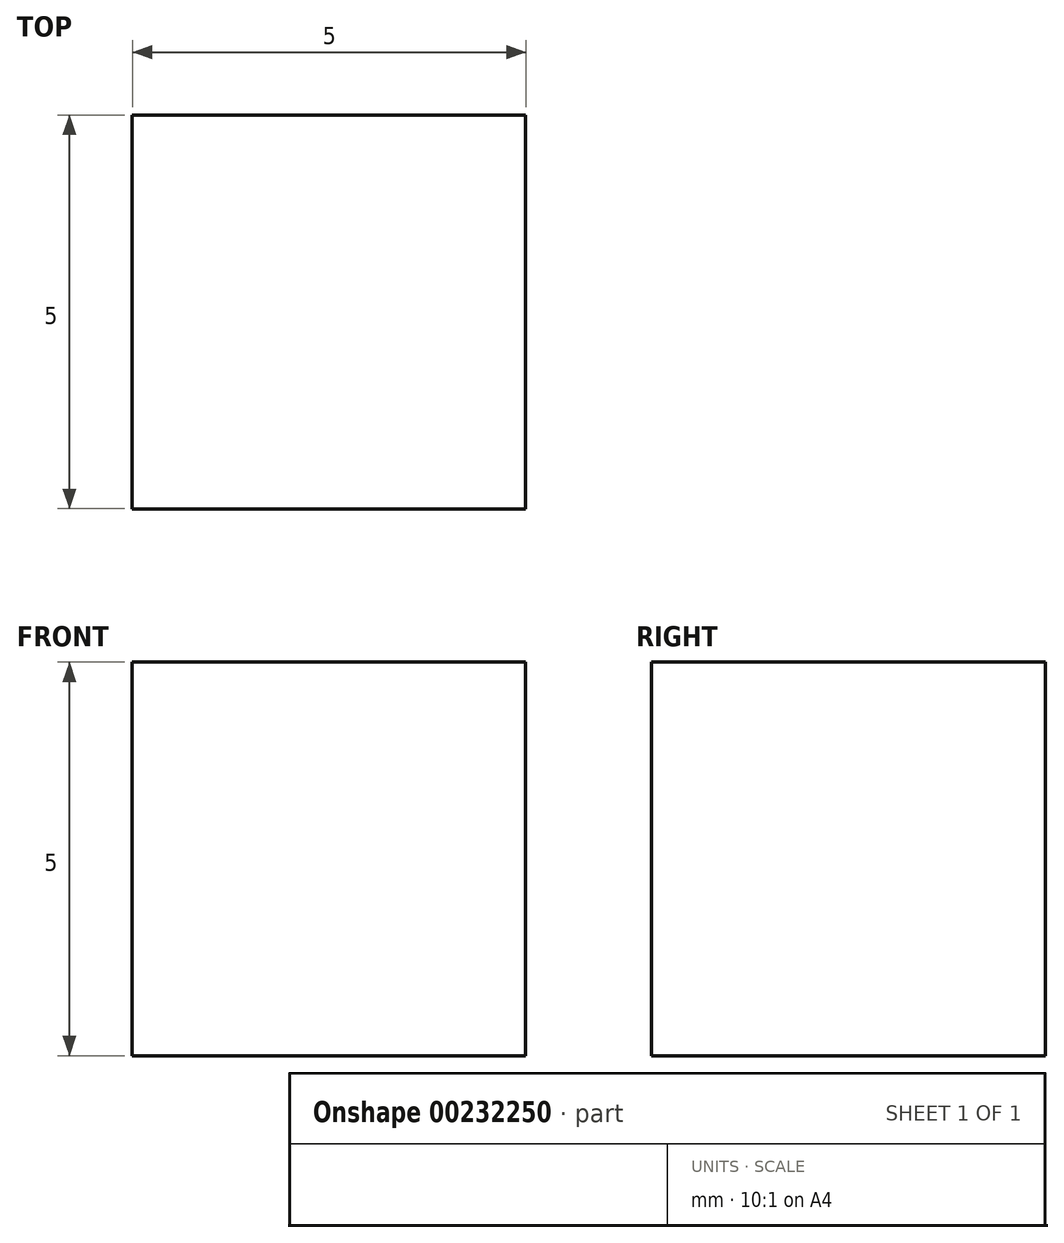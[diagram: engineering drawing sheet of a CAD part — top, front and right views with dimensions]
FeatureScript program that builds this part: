
annotation { "Feature Type Name" : "Feature", "Feature Type Description" : "" }
export const myFeature = defineFeature(function(context is Context, id is Id, definition is map)
    precondition{}
    {
        {
            var Q0;
            Q0=qCreatedBy(makeId("Top.planeOp"),FACE);
            var sketch = newSketch(context, id + "F0", { "sketchPlane" : qUnion([Q0])});
            skLineSegment(sketch, "E0.bottom", {"start": v(-14.38, 18.95) * mm, "end": v(-9.38, 18.95) * mm});
            skLineSegment(sketch, "E0.top", {"start": v(-14.38, 13.95) * mm, "end": v(-9.38, 13.95) * mm});
            skLineSegment(sketch, "E0.left", {"start": v(-14.38, 18.95) * mm, "end": v(-14.38, 13.95) * mm});
            skLineSegment(sketch, "E0.right", {"start": v(-9.38, 18.95) * mm, "end": v(-9.38, 13.95) * mm});
            skSolve(sketch);
        }
        {
            var Q0;
            Q0=makeQuery(id+"F0.imprint","IMPRINT",FACE,{"disambiguationData":[TD([[makeQuery(id+"F0.imprint","IMPRINT",EDGE,{"derivedFrom":sQuery(id+"F0.wireOp",EDGE,"E0.bottom")}),-1.0]])]});
            extrude(context, id + "F1", {"entities" : qUnion([Q0]), "depth" : 5 * mm});
        }
    });
